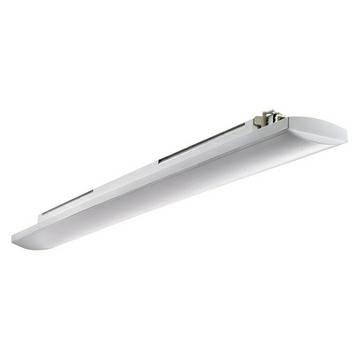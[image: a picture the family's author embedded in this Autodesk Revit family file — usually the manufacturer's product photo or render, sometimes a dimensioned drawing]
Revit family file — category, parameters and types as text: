
# Revit family: Lighting-Industriale-GEWISS-SMART[3]e-PLAFONIERA-LED_OPALE_800mm
name_source: partatom
category: Apparecchi per illuminazione
units: mm (PartAtom-declared; Revit-internal decimal feet)

## family parameters
Condiviso = No
Host = Superficie
Punto di calcolo locali = Sì
Quota connettore circolare = Usa diametro
Sorgente d'illuminazione = No
Taglio con vuoti quando caricato = No
Tipo di parte = Normale

## types (1)
- Lighting-Industriale-GEWISS-SMART[3]e-PLAFONIERA-LED_OPALE_800mm
    Alimentatore = Incluso
    Apparecchio a ridotta temperatura superficiale = Si
    Applicazione = Interno
    Cablaggio = Con connettore stagno Gw connect
    Cablaggio : = Stand alone
    Caratteristiche elettriche e gestione della luce = -
    Caratteristiche ottiche e illuminotecniche = -
    Carico apparente = 27 VA
    Catalogo = LIGHTING
    Certificazione DIN 18032-3 = Non disponibile
    Certificazioni e classificazioni = -
    Classe fotobiologica = -
    Classe isolamento = II
    Classificazione: = -
    Codice digitale univoco (Datamatrix) = Datamatrix
    Colore = Grigio RAL 7035
    Commenti sul wattaggio = 27W
    Contesto = Illuminazione di magazzini, parcheggi coperti e locali produttivi industriali
    Controllo abbagliamento e luminanza = UGR < 25 (4H/8H)
    Corpo = Policarbonato
    Descrizione = SMART3e 800 ON/OFF OPAL CRI80 4000K
    Dispositivo di protezione = DM 1KV / CM 2KV
    Durata di vita = L80B20(Tq25°C)=90.000h - L80B20(Tq40°C)=50.000h
    Failure rate alimentatore = F10 = 90.000 h a Tq 25°C/F10= 50.000 h a Tq 40°C
    Finitura colore = PC colorato in pasta RAL7035
    Fissaggio = Supporto in acciaio INOX
    Frequenza nominale (Hz) = 50/60 Hz
    Ganci = GEWISS  - ALLUMINIO
    Gancio di chiusura = -
    Garanzia = 5 anni
    Grado di protezione = IP66/IP69
    Gruppo ottico = Integrato nello schermo
    Guarnizioni = Sigillante depositato a CNC
    IDF = be846229-bf4a-4f5a-83b7-3e164804b7c0
    IDT = c14e9783-cfcd-4d50-ad03-d02503739214
    IPEA = -
    Immagine tipo = GWS3118P.jpg
    Inclinazione = Con staffa di fissaggio
    Indice di resa cromatica = CRI>80
    Informazioni generali = -
    Installazione e manutenzione = -
    Lampada = LED
    Lunghezza Lampada = 800 mm  [stored 2.62467 ft]
    Materiali = -
    Modello = GWS3120EP840
    Norma di riferimento = EN60598-1; IEC 62778; IEC62471
    Ottica = Opale diffondente
    Produttore = GEWISS S.p.A.
    Prospetto di default = 1219 mm
    Resistenza agli urti = IK08
    Resistenza al filo incandescente = 850 °C
    Scheda Tecnica = https://www.gewiss.com
    Schermo = Policarbonato stabilizzato agli UV
    Schermo. = Gewiss - Led Acceso
    Sistema di controllo = Stand Alone - On / Off
    Sistema di controllo : = ON / OFF
    Sostituibilità gruppo ottico = Non disponibile
    Sostituibilità piastra di cablaggio = Non disponibile
    Stampa 1_100 = Sì
    Stampa 1_200 = No
    Struttura = GEWISS - SMART 3 - GRIGIO
    Superficie massima esposta al vento : = -
    Temperatura di esercizio = -25 +40 °C
    Temperatura di stoccaggio = -25 +80 °C
    Tensione di alimentazione = 220 - 240 V
    Tipo di apparecchio = Apparecchio a LED per illuminazione generale
    Tipo di installazione e montaggio = Plafone - Parete - Sospensione
    Tipologia sorgente luminosa = LED - Non sostituibile
    Tolleranza cromatica = SDCM = 3
    URL = https://www.gewiss.com
    Vano di alimentazione = Integrato
    Versione file RFA = 21.4
    Viti esterne = -

note: [stored X ft] marks values corroborated as IEEE doubles in the binary element streams (Revit-internal decimal feet)
